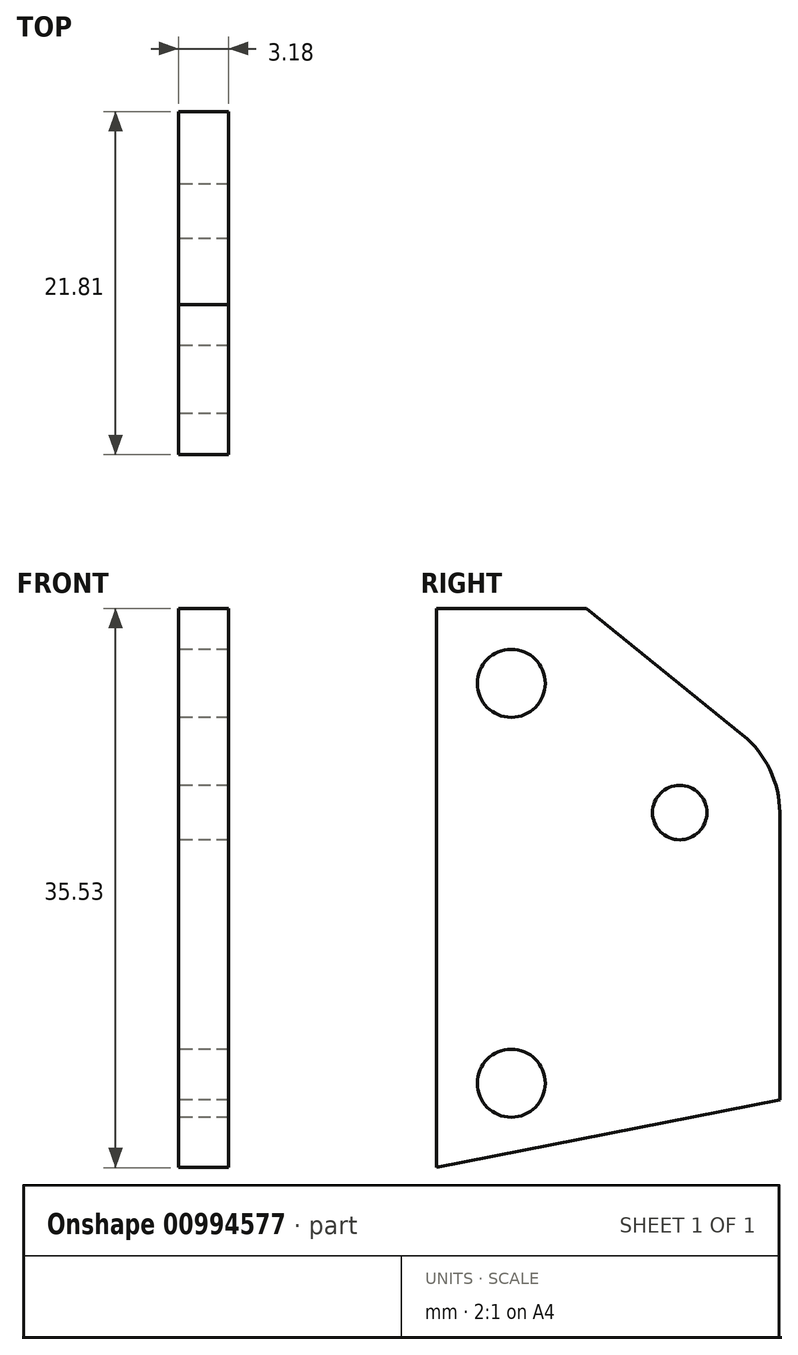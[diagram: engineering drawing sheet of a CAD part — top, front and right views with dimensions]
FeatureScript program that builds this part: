
annotation { "Feature Type Name" : "Feature", "Feature Type Description" : "" }
export const myFeature = defineFeature(function(context is Context, id is Id, definition is map)
    precondition{}
    {
        {
            var Q0;
            Q0=qCreatedBy(makeId("Right.planeOp"),FACE);
            var sketch = newSketch(context, id + "F0", { "sketchPlane" : qUnion([Q0])});
            skLineSegment(sketch, "E0", {"start": v(12.7, -17.46) * mm, "end": v(12.7, -52.99) * mm});
            skLineSegment(sketch, "E1", {"start": v(12.7, -52.99) * mm, "end": v(34.51, -48.68) * mm});
            skLineSegment(sketch, "E2", {"start": v(0, 0) * mm, "end": v(28.16, -30.44) * mm});
            skLineSegment(sketch, "E3", {"start": v(12.7, -17.46) * mm, "end": v(22.22, -17.46) * mm});
            skLineSegment(sketch, "E4", {"start": v(34.51, -48.68) * mm, "end": v(34.51, -30.44) * mm});
            skLineSegment(sketch, "E5", {"start": v(32.16, -25.5) * mm, "end": v(22.22, -17.46) * mm});
            skPoint(sketch, "E6.visualSharp", {"position": v(34.51, -27.4) * mm});
            skArc(sketch, "E6.filletArc", {"start": v(34.51, -30.44) * mm, "mid": v(33.9, -27.7) * mm, "end": v(32.16, -25.5) * mm});
            skCircle(sketch, "E7", {"center": v(28.16, -30.44) * mm, "radius": 2.16 * mm, "construction": true});
            skPoint(sketch, "E8", {"position": v(17.46, -22.23) * mm});
            skPoint(sketch, "E9", {"position": v(17.46, -47.62) * mm});
            skSolve(sketch);
        }
        {
            var Q0;
            {var subQ1=sQuery(id+"F0.wireOp",EDGE,"E0");Q0=makeQuery(id+"F0.imprint","IMPRINT",FACE,{"disambiguationData":[TD([[makeQuery(id+"F0.imprint","IMPRINT",EDGE,{"derivedFrom":subQ1}),1.0]])]});}
            extrude(context, id + "F1", {"entities" : qUnion([Q0]), "depth" : 3.17 * mm, "offsetDistance" : 25.4 * mm});
        }
        {
            var Q0;
            Q0=sQuery(id+"F0.wireOp",VERTEX,"E2.end");
            var Q1;
            Q1=makeQuery(id+"F1.opExtrude","SWEPT_BODY",BODY,{"disambiguationData":[OSD([sQuery(id+"F0.wireOp",EDGE,"E0"),sQuery(id+"F0.wireOp",EDGE,"E1"),sQuery(id+"F0.wireOp",EDGE,"E3"),sQuery(id+"F0.wireOp",EDGE,"E4"),sQuery(id+"F0.wireOp",EDGE,"E5"),sQuery(id+"F0.wireOp",EDGE,"E6.filletArc")])]});
            hole(context, id + "F2", {"style" : HoleStyle.SIMPLE, "endStyle" : HoleEndStyle.BLIND, "oppositeDirection" : true, "standardTappedOrClearance" : lookupTablePath({ "standard" : "ANSI", "engagement" : "75%", "pitch" : "32 tpi", "size" : "#8", "type" : "Tapped" }), "standardBlindInLast" : lookupTablePath({ "standard" : "ANSI", "fit" : "Normal", "engagement" : "75%", "pitch" : "32 tpi", "size" : "#8", "type" : "Clearance & tapped" }), "holeDiameter" : 3.45 * mm, "majorDiameter" : 4.17 * mm, "showTappedDepth" : true, "holeDepth" : 21.43 * mm, "isTappedThrough" : true, "tappedDepth" : 19.05 * mm, "tapClearance" : 3, "locations" : qUnion([Q0]), "scope" : qUnion([Q1])});
        }
        {
            var Q0;
            Q0=sQuery(id+"F0.wireOp",VERTEX,"E8");
            var Q1;
            Q1=sQuery(id+"F0.wireOp",VERTEX,"E9");
            var Q2;
            Q2=makeQuery(id+"F1.opExtrude","SWEPT_BODY",BODY,{"disambiguationData":[OSD([sQuery(id+"F0.wireOp",EDGE,"E0"),sQuery(id+"F0.wireOp",EDGE,"E1"),sQuery(id+"F0.wireOp",EDGE,"E3"),sQuery(id+"F0.wireOp",EDGE,"E4"),sQuery(id+"F0.wireOp",EDGE,"E5"),sQuery(id+"F0.wireOp",EDGE,"E6.filletArc")])]});
            hole(context, id + "F3", {"style" : HoleStyle.SIMPLE, "endStyle" : HoleEndStyle.BLIND, "oppositeDirection" : true, "standardTappedOrClearance" : lookupTablePath({ "fit" : "Normal (ASME)", "standard" : "ANSI", "size" : "#6", "type" : "Clearance" }), "standardBlindInLast" : lookupTablePath({ "fit" : "Normal", "standard" : "ANSI", "engagement" : "75%", "pitch" : "32 tpi", "size" : "#6", "type" : "Clearance & tapped" }), "holeDiameter" : 4.32 * mm, "majorDiameter" : 6.35 * mm, "holeDepth" : 15.88 * mm, "isTappedThrough" : true, "tappedDepth" : 19.05 * mm, "tapClearance" : 3, "locations" : qUnion([Q0, Q1]), "scope" : qUnion([Q2])});
        }
    });
